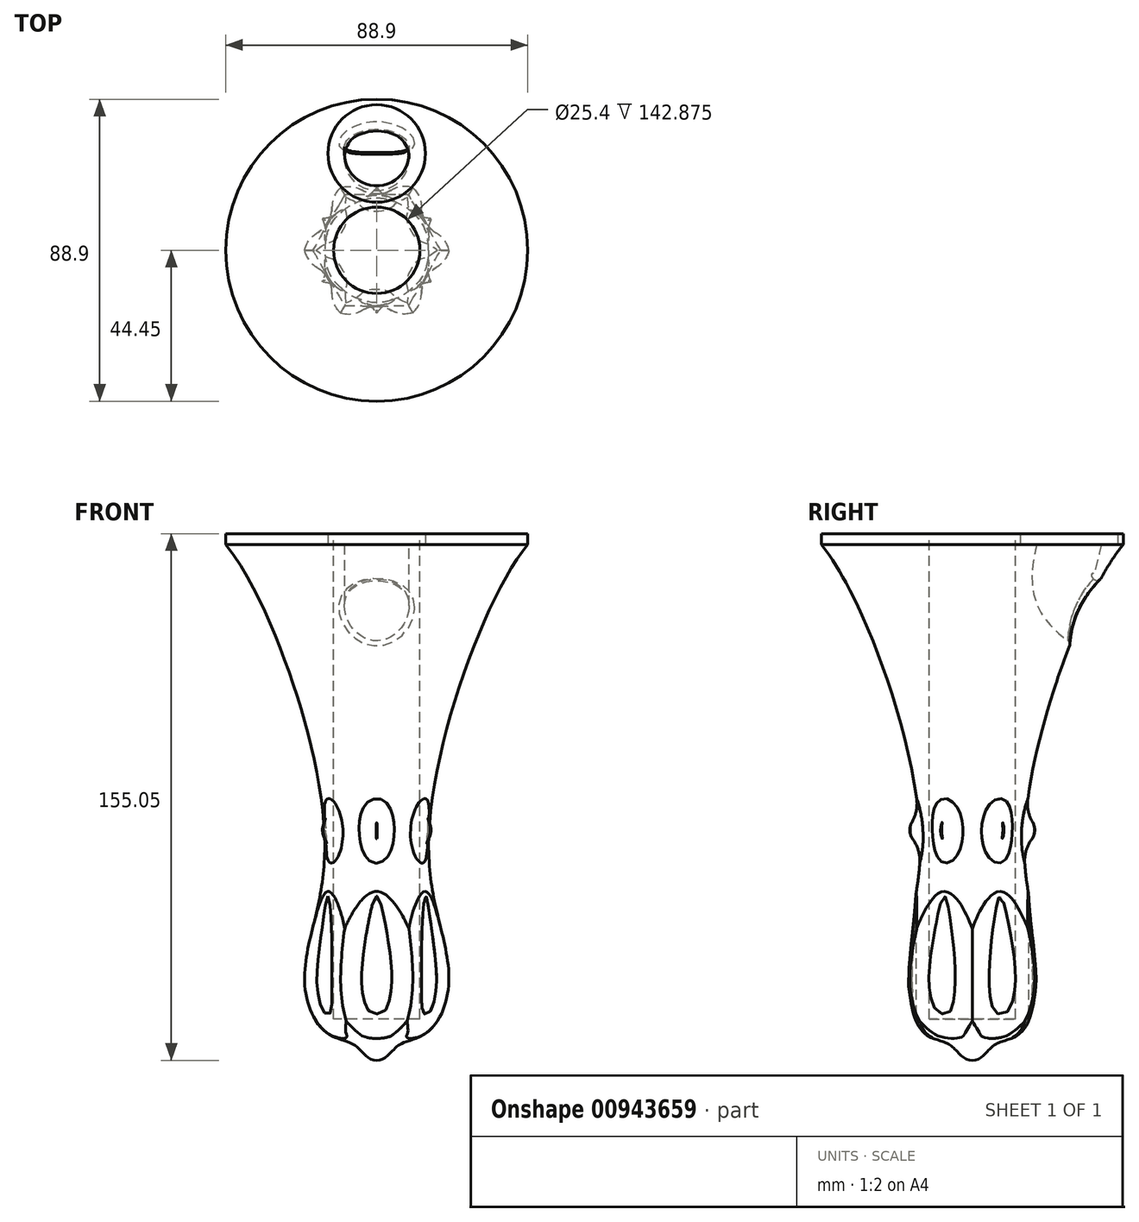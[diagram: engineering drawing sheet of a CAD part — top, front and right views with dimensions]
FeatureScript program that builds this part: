
annotation { "Feature Type Name" : "Feature", "Feature Type Description" : "" }
export const myFeature = defineFeature(function(context is Context, id is Id, definition is map)
    precondition{}
    {
        {
            var Q0;
            Q0=qCreatedBy(makeId("Front.planeOp"),FACE);
            var sketch = newSketch(context, id + "F0", { "sketchPlane" : qUnion([Q0])});
            skLineSegment(sketch, "E0", {"start": v(0, 0) * mm, "end": v(-12.7, 0) * mm});
            skLineSegment(sketch, "E1", {"start": v(-12.7, 0) * mm, "end": v(-12.7, 139.7) * mm});
            skLineSegment(sketch, "E2", {"start": v(-12.7, 139.7) * mm, "end": v(-44.45, 139.7) * mm});
            skPoint(sketch, "E3.4.internal.snap0", {"position": v(-6.35, 0) * mm});
            skFitSpline(sketch, "E3", {"points": [v(-44.45, 139.7) * mm, v(-15.3, 51.82) * mm, v(-21.5, 11.45) * mm, v(-14.37, -4.32) * mm, v(-6.35, -7.8) * mm, v(0, -12.17) * mm], "startDerivative": vector(103.36, -126) * mm, "endDerivative": vector(83.09, 0) * mm});
            skLineSegment(sketch, "E4", {"start": v(0, 0) * mm, "end": v(0, -12.17) * mm});
            skSolve(sketch);
        }
        {
            var Q0;
            Q0=qSketchRegion(id+"F0",true);
            var Q1;
            Q1=sQuery(id+"F0.wireOp",EDGE,"E4");
            revolve(context, id + "F1", {"surfaceOperationType" : NewSurfaceOperationType.NEW, "entities" : qUnion([Q0]), "axis" : qUnion([Q1]), "revolveType" : RevolveType.FULL});
        }
        {
            var Q0;
            Q0=qCreatedBy(makeId("Top.planeOp"),FACE);
            var sketch = newSketch(context, id + "F2", { "sketchPlane" : qUnion([Q0])});
            skCircle(sketch, "E5", {"center": v(0, -25.57) * mm, "radius": 9 * mm});
            skCircle(sketch, "E6.1.0", {"center": v(22.15, -12.79) * mm, "radius": 9 * mm});
            skCircle(sketch, "E6.2.0", {"center": v(22.15, 12.79) * mm, "radius": 9 * mm});
            skCircle(sketch, "E6.3.0", {"center": v(0, 25.57) * mm, "radius": 9 * mm});
            skCircle(sketch, "E6.4.0", {"center": v(-22.15, 12.79) * mm, "radius": 9 * mm});
            skCircle(sketch, "E6.5.0", {"center": v(-22.15, -12.79) * mm, "radius": 9 * mm});
            skPoint(sketch, "E6.center", {"position": v(0, 0) * mm});
            skSolve(sketch);
        }
        {
            var Q0;
            Q0=makeQuery(id+"F2.imprint","IMPRINT",FACE,{"disambiguationData":[TD([[makeQuery(id+"F2.imprint","IMPRINT",EDGE,{"derivedFrom":sQuery(id+"F2.wireOp",EDGE,"E5")}),1.0]])]});
            var Q1;
            Q1=makeQuery(id+"F2.imprint","IMPRINT",FACE,{"disambiguationData":[TD([[makeQuery(id+"F2.imprint","IMPRINT",EDGE,{"derivedFrom":sQuery(id+"F2.wireOp",EDGE,"E6.1.0")}),1.0]])]});
            var Q2;
            Q2=makeQuery(id+"F2.imprint","IMPRINT",FACE,{"disambiguationData":[TD([[makeQuery(id+"F2.imprint","IMPRINT",EDGE,{"derivedFrom":sQuery(id+"F2.wireOp",EDGE,"E6.5.0")}),1.0]])]});
            var Q3;
            Q3=makeQuery(id+"F2.imprint","IMPRINT",FACE,{"disambiguationData":[TD([[makeQuery(id+"F2.imprint","IMPRINT",EDGE,{"derivedFrom":sQuery(id+"F2.wireOp",EDGE,"E6.4.0")}),1.0]])]});
            var Q4;
            Q4=makeQuery(id+"F2.imprint","IMPRINT",FACE,{"disambiguationData":[TD([[makeQuery(id+"F2.imprint","IMPRINT",EDGE,{"derivedFrom":sQuery(id+"F2.wireOp",EDGE,"E6.2.0")}),1.0]])]});
            var Q5;
            Q5=makeQuery(id+"F2.imprint","IMPRINT",FACE,{"disambiguationData":[TD([[makeQuery(id+"F2.imprint","IMPRINT",EDGE,{"derivedFrom":sQuery(id+"F2.wireOp",EDGE,"E6.3.0")}),1.0]])]});
            extrude(context, id + "F3", {"entities" : qUnion([Q0, Q1, Q2, Q3, Q4, Q5]), "operationType" : NewBodyOperationType.REMOVE, "depth" : 54.1 * mm, "offsetDistance" : 25.4 * mm, "hasSecondDirection" : true, "secondDirectionOppositeDirection" : true, "secondDirectionDepth" : 25.4 * mm});
        }
        {
            var Q0;
            Q0=makeQuery(id+"F3.boolean.opBoolean","COPY",FACE,{"derivedFrom":makeQuery(id+"F3.opExtrude","SWEPT_FACE",FACE,{"disambiguationData":[OSD([sQuery(id+"F2.wireOp",EDGE,"E6.1.0")])]})});
            var Q1;
            Q1=makeQuery(id+"F3.boolean.opBoolean","COPY",FACE,{"derivedFrom":makeQuery(id+"F3.opExtrude","SWEPT_FACE",FACE,{"disambiguationData":[OSD([sQuery(id+"F2.wireOp",EDGE,"E6.2.0")])]})});
            var Q2;
            Q2=makeQuery(id+"F3.boolean.opBoolean","INTERSECT",EDGE,{"derivedFrom":[makeQuery(id+"F1.opRevolve","SWEPT_FACE",FACE,{"disambiguationData":[OSD([sQuery(id+"F0.wireOp",EDGE,"E3")])]}),makeQuery(id+"F3.opExtrude","SWEPT_FACE",FACE,{"disambiguationData":[OSD([sQuery(id+"F2.wireOp",EDGE,"E6.3.0")])]})]});
            var Q3;
            Q3=makeQuery(id+"F3.boolean.opBoolean","COPY",FACE,{"derivedFrom":makeQuery(id+"F3.opExtrude","SWEPT_FACE",FACE,{"disambiguationData":[OSD([sQuery(id+"F2.wireOp",EDGE,"E6.4.0")])]})});
            var Q4;
            Q4=makeQuery(id+"F3.boolean.opBoolean","COPY",FACE,{"derivedFrom":makeQuery(id+"F3.opExtrude","SWEPT_FACE",FACE,{"disambiguationData":[OSD([sQuery(id+"F2.wireOp",EDGE,"E6.5.0")])]})});
            var Q5;
            Q5=makeQuery(id+"F3.boolean.opBoolean","COPY",FACE,{"derivedFrom":makeQuery(id+"F3.opExtrude","SWEPT_FACE",FACE,{"disambiguationData":[OSD([sQuery(id+"F2.wireOp",EDGE,"E5")])]})});
            fillet(context, id + "F4", {"entities" : qUnion([Q0, Q1, Q2, Q3, Q4, Q5]), "radius" : 7.62 * mm, "tangentPropagation" : true, "allowEdgeOverflow" : false});
        }
        {
            var Q0;
            Q0=qCreatedBy(makeId("Top.planeOp"),FACE);
            cPlane(context, id + "F5", {"entities" : qUnion([Q0]), "cplaneType" : CPlaneType.OFFSET, "offset" : 55.63 * mm, "width" : 152.4 * mm, "height" : 152.4 * mm});
        }
        {
            var Q0;
            Q0=qCreatedBy(id+"F5.planeOp",FACE);
            var sketch = newSketch(context, id + "F6", { "sketchPlane" : qUnion([Q0])});
            skEllipse(sketch, "E7", {"center": v(0, -13.97) * mm, "majorRadius": 4.46 * mm, "minorRadius": 0.76 * mm, "majorAxis": v(0, -1)});
            skEllipse(sketch, "E8.1.0", {"center": v(12.1, -6.99) * mm, "majorRadius": 4.46 * mm, "minorRadius": 0.76 * mm, "majorAxis": v(0.87, -0.5)});
            skEllipse(sketch, "E8.2.0", {"center": v(12.1, 6.99) * mm, "majorRadius": 4.46 * mm, "minorRadius": 0.76 * mm, "majorAxis": v(0.87, 0.5)});
            skEllipse(sketch, "E8.3.0", {"center": v(0, 13.97) * mm, "majorRadius": 4.46 * mm, "minorRadius": 0.76 * mm, "majorAxis": v(0, 1)});
            skEllipse(sketch, "E8.4.0", {"center": v(-12.1, 6.99) * mm, "majorRadius": 4.46 * mm, "minorRadius": 0.76 * mm, "majorAxis": v(-0.87, 0.5)});
            skEllipse(sketch, "E8.5.0", {"center": v(-12.1, -6.99) * mm, "majorRadius": 4.46 * mm, "minorRadius": 0.76 * mm, "majorAxis": v(-0.87, -0.5)});
            skPoint(sketch, "E8.center", {"position": v(0, 0) * mm});
            skLineSegment(sketch, "E9", {"start": v(-12.1, -6.99) * mm, "end": v(-11.72, -7.64) * mm});
            skLineSegment(sketch, "E10", {"start": v(-12.1, -6.99) * mm, "end": v(-12.48, -6.33) * mm});
            skLineSegment(sketch, "E11", {"start": v(0, -13.97) * mm, "end": v(-0.76, -13.97) * mm});
            skLineSegment(sketch, "E12", {"start": v(0, -13.97) * mm, "end": v(0.76, -13.97) * mm});
            skLineSegment(sketch, "E13", {"start": v(12.1, -6.99) * mm, "end": v(11.72, -7.64) * mm});
            skLineSegment(sketch, "E14", {"start": v(12.1, -6.99) * mm, "end": v(12.48, -6.33) * mm});
            skLineSegment(sketch, "E15", {"start": v(12.1, 6.99) * mm, "end": v(12.48, 6.33) * mm});
            skLineSegment(sketch, "E16", {"start": v(12.1, 6.99) * mm, "end": v(11.72, 7.64) * mm});
            skLineSegment(sketch, "E17", {"start": v(0, 13.97) * mm, "end": v(-0.76, 13.97) * mm});
            skLineSegment(sketch, "E18", {"start": v(0, 13.97) * mm, "end": v(0.76, 13.97) * mm});
            skLineSegment(sketch, "E19", {"start": v(-12.1, 6.99) * mm, "end": v(-12.48, 6.33) * mm});
            skLineSegment(sketch, "E20", {"start": v(-12.1, 6.99) * mm, "end": v(-11.72, 7.64) * mm});
            skSolve(sketch);
        }
        {
            var Q0;
            {var subQ0=sQuery(id+"F6.wireOp",EDGE,"E9");Q0=makeQuery(id+"F6.imprint","IMPRINT",FACE,{"disambiguationData":[TD([[makeQuery(id+"F6.imprint","IMPRINT",EDGE,{"derivedFrom":subQ0}),-1.0]])]});}
            var Q1;
            Q1=sQuery(id+"F6.wireOp",EDGE,"E9");
            revolve(context, id + "F7", {"operationType" : NewBodyOperationType.ADD, "surfaceOperationType" : NewSurfaceOperationType.NEW, "entities" : qUnion([Q0]), "axis" : qUnion([Q1]), "revolveType" : RevolveType.FULL});
        }
        {
            var Q0;
            {var subQ0=sQuery(id+"F6.wireOp",EDGE,"E11");Q0=makeQuery(id+"F6.imprint","IMPRINT",FACE,{"disambiguationData":[TD([[makeQuery(id+"F6.imprint","IMPRINT",EDGE,{"derivedFrom":subQ0}),1.0]])]});}
            var Q1;
            Q1=sQuery(id+"F6.wireOp",EDGE,"E12");
            revolve(context, id + "F8", {"operationType" : NewBodyOperationType.ADD, "surfaceOperationType" : NewSurfaceOperationType.NEW, "entities" : qUnion([Q0]), "axis" : qUnion([Q1]), "revolveType" : RevolveType.FULL});
        }
        {
            var Q0;
            {var subQ0=sQuery(id+"F6.wireOp",EDGE,"E13");Q0=makeQuery(id+"F6.imprint","IMPRINT",FACE,{"disambiguationData":[TD([[makeQuery(id+"F6.imprint","IMPRINT",EDGE,{"derivedFrom":subQ0}),-1.0]])]});}
            var Q1;
            Q1=sQuery(id+"F6.wireOp",EDGE,"E13");
            revolve(context, id + "F9", {"operationType" : NewBodyOperationType.ADD, "surfaceOperationType" : NewSurfaceOperationType.NEW, "entities" : qUnion([Q0]), "axis" : qUnion([Q1]), "revolveType" : RevolveType.FULL});
        }
        {
            var Q0;
            {var subQ0=sQuery(id+"F6.wireOp",EDGE,"E15");Q0=makeQuery(id+"F6.imprint","IMPRINT",FACE,{"disambiguationData":[TD([[makeQuery(id+"F6.imprint","IMPRINT",EDGE,{"derivedFrom":subQ0}),-1.0]])]});}
            var Q1;
            Q1=sQuery(id+"F6.wireOp",EDGE,"E16");
            revolve(context, id + "F10", {"operationType" : NewBodyOperationType.ADD, "surfaceOperationType" : NewSurfaceOperationType.NEW, "entities" : qUnion([Q0]), "axis" : qUnion([Q1]), "revolveType" : RevolveType.FULL});
        }
        {
            var Q0;
            {var subQ0=sQuery(id+"F6.wireOp",EDGE,"E17");Q0=makeQuery(id+"F6.imprint","IMPRINT",FACE,{"disambiguationData":[TD([[makeQuery(id+"F6.imprint","IMPRINT",EDGE,{"derivedFrom":subQ0}),1.0]])]});}
            var Q1;
            Q1=sQuery(id+"F6.wireOp",EDGE,"E17");
            revolve(context, id + "F11", {"operationType" : NewBodyOperationType.ADD, "surfaceOperationType" : NewSurfaceOperationType.NEW, "entities" : qUnion([Q0]), "axis" : qUnion([Q1]), "revolveType" : RevolveType.FULL});
        }
        {
            var Q0;
            {var subQ0=sQuery(id+"F6.wireOp",EDGE,"E19");Q0=makeQuery(id+"F6.imprint","IMPRINT",FACE,{"disambiguationData":[TD([[makeQuery(id+"F6.imprint","IMPRINT",EDGE,{"derivedFrom":subQ0}),1.0]])]});}
            var Q1;
            Q1=sQuery(id+"F6.wireOp",EDGE,"E20");
            revolve(context, id + "F12", {"operationType" : NewBodyOperationType.ADD, "surfaceOperationType" : NewSurfaceOperationType.NEW, "entities" : qUnion([Q0]), "axis" : qUnion([Q1]), "revolveType" : RevolveType.FULL});
        }
        {
            var Q0;
            Q0=makeQuery(id+"F7.boolean.opBoolean","INTERSECT",EDGE,{"derivedFrom":[makeQuery(id+"F4.opFillet","SPLIT",FACE,{"disambiguationData":[OD(1.0)],"derivedFrom":makeQuery(id+"F1.opRevolve","SWEPT_FACE",FACE,{"disambiguationData":[OSD([sQuery(id+"F0.wireOp",EDGE,"E3")])]})}),makeQuery(id+"F7.opRevolve","SWEPT_FACE",FACE,{"disambiguationData":[OSD([sQuery(id+"F6.wireOp",EDGE,"E8.5.0")])]})]});
            var Q1;
            Q1=makeQuery(id+"F8.boolean.opBoolean","INTERSECT",EDGE,{"derivedFrom":[makeQuery(id+"F4.opFillet","SPLIT",FACE,{"disambiguationData":[OD(1.0)],"derivedFrom":makeQuery(id+"F1.opRevolve","SWEPT_FACE",FACE,{"disambiguationData":[OSD([sQuery(id+"F0.wireOp",EDGE,"E3")])]})}),makeQuery(id+"F8.opRevolve","SWEPT_FACE",FACE,{"disambiguationData":[OSD([sQuery(id+"F6.wireOp",EDGE,"E7")])]})]});
            var Q2;
            Q2=makeQuery(id+"F9.boolean.opBoolean","INTERSECT",EDGE,{"derivedFrom":[makeQuery(id+"F4.opFillet","SPLIT",FACE,{"disambiguationData":[OD(1.0)],"derivedFrom":makeQuery(id+"F1.opRevolve","SWEPT_FACE",FACE,{"disambiguationData":[OSD([sQuery(id+"F0.wireOp",EDGE,"E3")])]})}),makeQuery(id+"F9.opRevolve","SWEPT_FACE",FACE,{"disambiguationData":[OSD([sQuery(id+"F6.wireOp",EDGE,"E8.1.0")])]})]});
            var Q3;
            Q3=makeQuery(id+"F10.boolean.opBoolean","INTERSECT",EDGE,{"derivedFrom":[makeQuery(id+"F4.opFillet","SPLIT",FACE,{"disambiguationData":[OD(1.0)],"derivedFrom":makeQuery(id+"F1.opRevolve","SWEPT_FACE",FACE,{"disambiguationData":[OSD([sQuery(id+"F0.wireOp",EDGE,"E3")])]})}),makeQuery(id+"F10.opRevolve","SWEPT_FACE",FACE,{"disambiguationData":[OSD([sQuery(id+"F6.wireOp",EDGE,"E8.2.0")])]})]});
            var Q4;
            Q4=makeQuery(id+"F11.boolean.opBoolean","INTERSECT",EDGE,{"derivedFrom":[makeQuery(id+"F4.opFillet","SPLIT",FACE,{"disambiguationData":[OD(1.0)],"derivedFrom":makeQuery(id+"F1.opRevolve","SWEPT_FACE",FACE,{"disambiguationData":[OSD([sQuery(id+"F0.wireOp",EDGE,"E3")])]})}),makeQuery(id+"F11.opRevolve","SWEPT_FACE",FACE,{"disambiguationData":[OSD([sQuery(id+"F6.wireOp",EDGE,"E8.3.0")])]})]});
            var Q5;
            Q5=makeQuery(id+"F12.boolean.opBoolean","INTERSECT",EDGE,{"derivedFrom":[makeQuery(id+"F4.opFillet","SPLIT",FACE,{"disambiguationData":[OD(1.0)],"derivedFrom":makeQuery(id+"F1.opRevolve","SWEPT_FACE",FACE,{"disambiguationData":[OSD([sQuery(id+"F0.wireOp",EDGE,"E3")])]})}),makeQuery(id+"F12.opRevolve","SWEPT_FACE",FACE,{"disambiguationData":[OSD([sQuery(id+"F6.wireOp",EDGE,"E8.4.0")])]})]});
            fillet(context, id + "F13", {"entities" : qUnion([Q0, Q1, Q2, Q3, Q4, Q5]), "radius" : 10.67 * mm, "tangentPropagation" : true, "allowEdgeOverflow" : false});
        }
        {
            var Q0;
            Q0=makeQuery(id+"F1.opRevolve","SWEPT_FACE",FACE,{"disambiguationData":[OSD([sQuery(id+"F0.wireOp",EDGE,"E2")])]});
            var sketch = newSketch(context, id + "F14", { "sketchPlane" : qUnion([Q0])});
            skLineSegment(sketch, "E21", {"start": v(0, 44.45) * mm, "end": v(0, 0) * mm});
            skLineSegment(sketch, "E22", {"start": v(0, -3.26) * mm, "end": v(0, 28.5) * mm});
            skCircle(sketch, "E23", {"center": v(0, 28.5) * mm, "radius": 9.53 * mm});
            skLineSegment(sketch, "E24", {"start": v(0, 44.45) * mm, "end": v(-12.82, 44.45) * mm});
            skLineSegment(sketch, "E25", {"start": v(-12.73, 50.11) * mm, "end": v(11.02, 50.11) * mm});
            skSolve(sketch);
        }
        {
            var Q0;
            Q0=makeQuery(id+"F1.opRevolve","SWEPT_FACE",FACE,{"disambiguationData":[OSD([sQuery(id+"F0.wireOp",EDGE,"E0")])]});
            var sketch = newSketch(context, id + "F15", { "sketchPlane" : qUnion([Q0])});
            skCircle(sketch, "E26", {"center": v(0, 0) * mm, "radius": 12.7 * mm});
            skSolve(sketch);
        }
        {
            var Q0;
            Q0 = qSketchRegion(id + "F15", true);
            extrude(context, id + "F16", {"entities" : qUnion([Q0]), "operationType" : NewBodyOperationType.REMOVE, "depth" : 224.28 * mm, "offsetDistance" : 25.4 * mm});
        }
        {
            var Q0;
            Q0=qCreatedBy(makeId("Right.planeOp"),FACE);
            var sketch = newSketch(context, id + "F17", { "sketchPlane" : qUnion([Q0])});
            skFitSpline(sketch, "E27", {"points": [v(28.22, 139.87) * mm, v(27.86, 124.66) * mm, v(39.88, 114.4) * mm], "startDerivative": vector(-9.28, -40.03) * mm, "endDerivative": vector(28.2, -17.85) * mm});
            skSolve(sketch);
        }
        {
            var Q0;
            {var subQ0=sQuery(id+"F14.wireOp",EDGE,"E22");var subQ1=sQuery(id+"F14.wireOp",EDGE,"E21");var subQ2=makeQuery(id+"F14.imprint","INTERSECT",VERTEX,{"derivedFrom":[subQ1,subQ0]});Q0=makeQuery(id+"F14.imprint","IMPRINT",FACE,{"disambiguationData":[TD([[makeQuery(id+"F14.imprint","IMPRINT",EDGE,{"disambiguationData":[TD([[subQ2,1.0]])],"derivedFrom":subQ1}),1.0]])]});}
            var Q1;
            {var subQ0=sQuery(id+"F14.wireOp",EDGE,"E22");var subQ1=sQuery(id+"F14.wireOp",EDGE,"E21");var subQ2=makeQuery(id+"F14.imprint","INTERSECT",VERTEX,{"derivedFrom":[subQ1,subQ0]});Q1=makeQuery(id+"F14.imprint","IMPRINT",FACE,{"disambiguationData":[TD([[makeQuery(id+"F14.imprint","IMPRINT",EDGE,{"disambiguationData":[TD([[subQ2,1.0]])],"derivedFrom":subQ1}),-1.0]])]});}
            var Q2;
            Q2=sQuery(id+"F17.wireOp",EDGE,"E27");
            sweep(context, id + "F18", {"operationType" : NewBodyOperationType.REMOVE, "profiles" : qUnion([Q0, Q1]), "path" : qUnion([Q2])});
        }
        {
            var Q0;
            Q0=makeQuery(id+"F18.boolean.opBoolean","INTERSECT",EDGE,{"derivedFrom":[makeQuery(id+"F4.opFillet","SPLIT",FACE,{"disambiguationData":[OD(1.0)],"derivedFrom":makeQuery(id+"F1.opRevolve","SWEPT_FACE",FACE,{"disambiguationData":[OSD([sQuery(id+"F0.wireOp",EDGE,"E3")])]})}),makeQuery(id+"F18.opSweep","SWEPT_FACE",FACE,{"disambiguationData":[OSD([sQuery(id+"F14.wireOp",EDGE,"E23"),sQuery(id+"F17.wireOp",EDGE,"E27")])]})]});
            fillet(context, id + "F19", {"entities" : qUnion([Q0]), "radius" : 1.27 * mm, "tangentPropagation" : true, "allowEdgeOverflow" : false});
        }
        {
            var Q0;
            Q0=makeQuery(id+"F1.opRevolve","SWEPT_FACE",FACE,{"disambiguationData":[OSD([sQuery(id+"F0.wireOp",EDGE,"E2")])]});
            var sketch = newSketch(context, id + "F20", { "sketchPlane" : qUnion([Q0])});
            skCircle(sketch, "E28", {"center": v(0, 0) * mm, "radius": 12.7 * mm});
            skCircle(sketch, "E29", {"center": v(0, 28.5) * mm, "radius": 9.53 * mm});
            skCircle(sketch, "E30", {"center": v(0, 0) * mm, "radius": 44.45 * mm});
            skCircle(sketch, "E31", {"center": v(0, 28.5) * mm, "radius": 14.34 * mm});
            skSolve(sketch);
        }
        {
            var Q0;
            Q0 = qSketchRegion(id + "F20", true);
            extrude(context, id + "F21", {"entities" : qUnion([Q0]), "operationType" : NewBodyOperationType.ADD, "depth" : 3.17 * mm, "offsetDistance" : 25.4 * mm});
        }
    });
